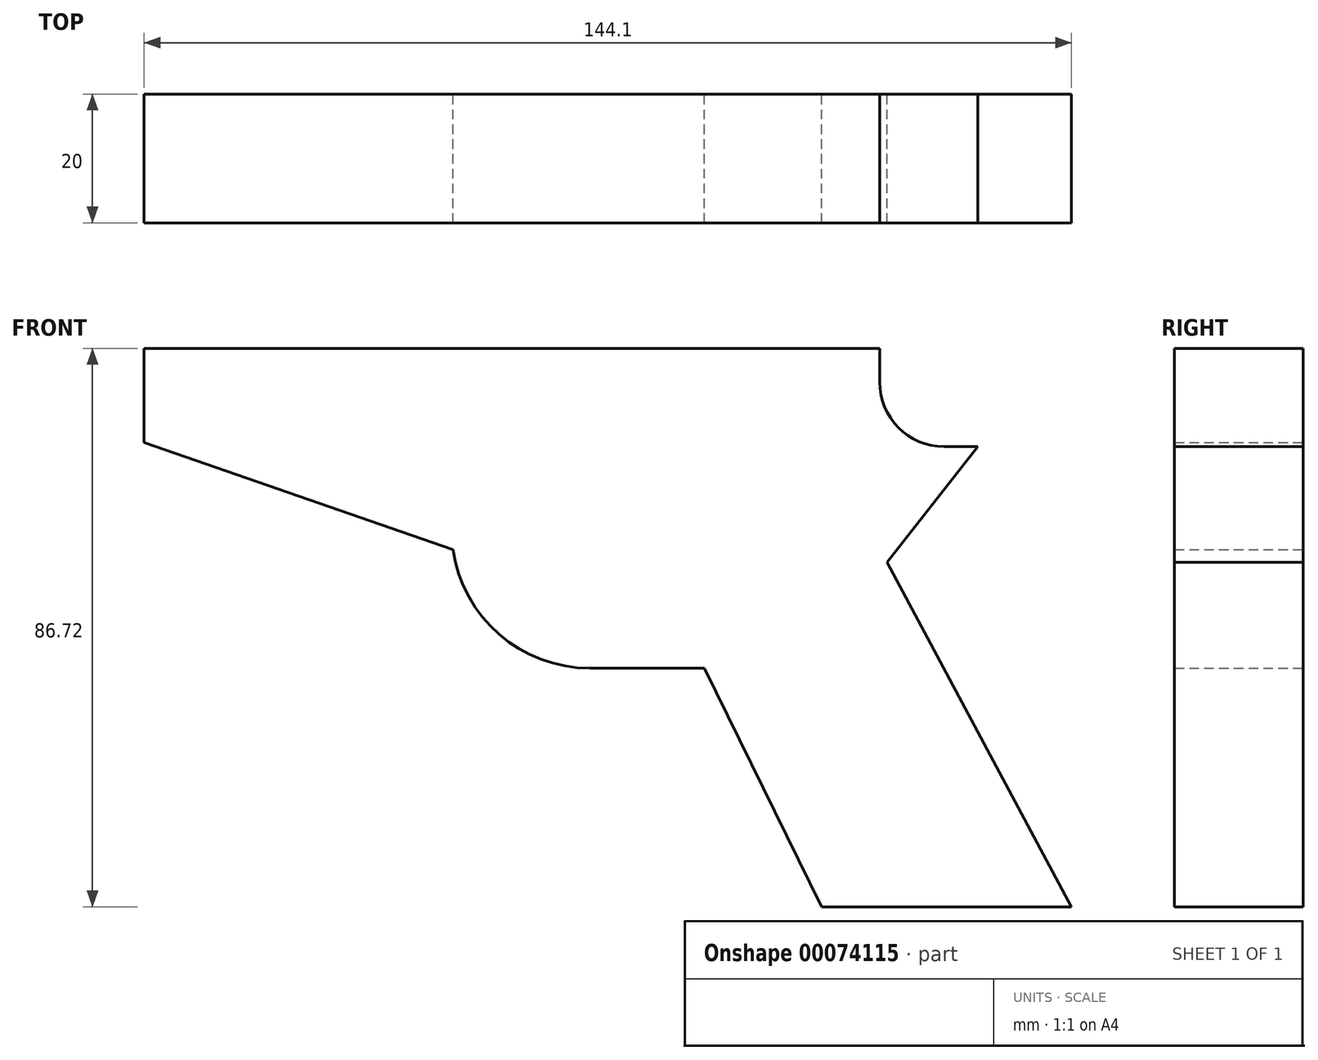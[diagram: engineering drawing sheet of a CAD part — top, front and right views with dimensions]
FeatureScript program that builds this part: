
annotation { "Feature Type Name" : "Feature", "Feature Type Description" : "" }
export const myFeature = defineFeature(function(context is Context, id is Id, definition is map)
    precondition{}
    {
        {
            var Q0;
            Q0=qCreatedBy(makeId("Front.planeOp"),FACE);
            var sketch = newSketch(context, id + "F0", { "sketchPlane" : qUnion([Q0])});
            skLineSegment(sketch, "E0", {"start": v(47.28, 50.5) * mm, "end": v(-67.02, 50.5) * mm});
            skLineSegment(sketch, "E1", {"start": v(47.28, 50.5) * mm, "end": v(47.28, 35.25) * mm});
            skLineSegment(sketch, "E2", {"start": v(47.28, 35.25) * mm, "end": v(62.52, 35.25) * mm});
            skLineSegment(sketch, "E3", {"start": v(62.52, 35.25) * mm, "end": v(48.42, 17.26) * mm});
            skLineSegment(sketch, "E4", {"start": v(48.42, 17.26) * mm, "end": v(77.08, -36.23) * mm});
            skLineSegment(sketch, "E5", {"start": v(77.08, -36.23) * mm, "end": v(38.23, -36.23) * mm});
            skLineSegment(sketch, "E6", {"start": v(38.23, -36.23) * mm, "end": v(20, 0.83) * mm});
            skLineSegment(sketch, "E7", {"start": v(-67.02, 50.5) * mm, "end": v(-67.02, 35.85) * mm});
            skLineSegment(sketch, "E8", {"start": v(-67.02, 35.85) * mm, "end": v(-19.01, 19.25) * mm});
            skLineSegment(sketch, "E9", {"start": v(20, 0.83) * mm, "end": v(2.22, 0.83) * mm});
            skArc(sketch, "E10", {"start": v(-19.01, 19.25) * mm, "mid": v(-11.84, 6.08) * mm, "end": v(2.22, 0.83) * mm});
            skSolve(sketch);
        }
        {
            var Q0;
            Q0=makeQuery(id+"F0.imprint","IMPRINT",FACE,{"disambiguationData":[TD([[makeQuery(id+"F0.imprint","IMPRINT",EDGE,{"derivedFrom":sQuery(id+"F0.wireOp",EDGE,"E0")}),1.0]])]});
            extrude(context, id + "F1", {"entities" : qUnion([Q0]), "depth" : 20 * mm});
        }
        {
            var Q0;
            Q0=makeQuery(id+"F1.opExtrude","SWEPT_EDGE",EDGE,{"disambiguationData":[OSD([sQuery(id+"F0.wireOp",EDGE,"E1"),sQuery(id+"F0.wireOp",EDGE,"E2")])]});
            fillet(context, id + "F2", {"entities" : qUnion([Q0]), "radius" : 10 * mm, "tangentPropagation" : true, "allowEdgeOverflow" : false});
        }
    });
